SOLIDWORKS PART (.sldprt)
format: sldprt  version: not decoded by parser v0  size: 369,664 bytes
history: native  units: mm
features: sketch x10, cut_extrude x8, material x1, extrude x1 (+13 scaffold rows collapsed)
feature tree (33):
  scaffold x13  (default folders/planes/origin — collapsed)
  material  "Material <not specified>"
  sketch  "Sketch1"  dims[D1=0.0mm]
  extrude  "Boss-Extrude1"  Depth=3mm
  sketch  "Sketch3"
  sketch  "Sketch4"
  cut_extrude  "Cut-Extrude1"  [1 undecoded]
  sketch  "Sketch5"  dims[D1=0.0mm D2=0.0mm]
  cut_extrude  "Cut-Extrude2"  [1 undecoded]
  sketch  "Sketch6"  dims[D1=0.0mm]
  cut_extrude  "Cut-Extrude3"  [1 undecoded]
  sketch  "Sketch7"  dims[D1=6.0mm]
  cut_extrude  "Cut-Extrude4"  [1 undecoded]
  sketch  "Sketch8"
  cut_extrude  "Cut-Extrude5"  [1 undecoded]
  sketch  "Sketch9"
  cut_extrude  "Cut-Extrude6"  [1 undecoded]
  sketch  "Sketch10"
  cut_extrude  "Cut-Extrude7"  [1 undecoded]
  sketch  "Sketch11"  dims[D1=~15.853306mm]
  cut_extrude  "Cut-Extrude8"  [1 undecoded]
decode coverage: 6 of 19 modeling features carry decoded parameters
note: ~ marks probable driven/reference dimensions
note: 8 parameter values undecoded
summary: no parameter record found for 8 features
note: suppression state not decoded; provenance and decode notes live in map.json
